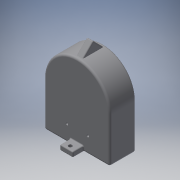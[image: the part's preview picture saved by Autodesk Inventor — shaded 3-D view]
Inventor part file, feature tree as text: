
AUTODESK INVENTOR PART (.ipt)
format: ipt  version: 2018 (Build 220112000, 112)  size: 288,768 bytes
history: native  units: in
note: dims shown in document units (in); Inventor stores cm internally (conversion verified against a paired STEP export)
features: fillet x9, extrude x7, sketch x6, reference x4, plane x1
ambient origin geometry x8: Origin, YZ Plane, XZ Plane, XY Plane, X Axis, Y Axis, Z Axis, Center Point
bodies: Solid1 (feature_tree)
feature tree (27):
  extrude  "Extrusion1"  Depth=1.0in TaperAngle=0.0deg
  extrude  "Extrusion4"  Depth=0.4in TaperAngle=0.0deg
  extrude  "Extrusion5"  Depth=0.1772in
  extrude  "Extrusion6"  Depth=0.25in
  extrude  "Extrusion8"  Depth=0.197in
  plane  "Work Plane1"
  extrude  "Extrusion9"  Depth=0.5in
  extrude  "Extrusion10"  Depth=0.25in
  fillet  "Fillet1"  Radius=0.5in
  fillet  "Fillet2"  Radius=0.197in
  fillet  "Fillet3"  Radius=0.15in
  fillet  "Fillet4"  Radius=0.1378in
  fillet  "Fillet5"  Radius=0.4in
  fillet  "Fillet6"  [1 undecoded]
  fillet  "Fillet7"  Radius=0.1065in
  fillet  "Fillet8"  Radius=0.787in
  fillet  "Fillet9"  Radius=0.394in
  sketch  "Sketch1"  dims[d0=2.5in d1=1.0in d2=0.0in]
  reference  "Reference1"
  sketch  "Sketch2"  dims[d9=0.197in d10=0.4in d11=0.0in]
  reference  "Reference2"
  sketch  "Sketch4"  dims[d12=0.15in d13=0.1772in]
  sketch  "Sketch7"  dims[d14=0.4in d15=0.0in d16=0.25in]
  sketch  "Sketch8"  dims[d17=0.5in d18=0.197in]
  sketch  "Sketch9"  dims[d19=0.4in d20=0.0in d25=0.5in d26=0.25in d27=0.5in d28=0.197in d29=0.15in d30=0.1378in d31=0.4in d32=0.0in d33=-1.25in d34=0.1065in d35=0.787in d36=0.394in d37=0.394in d38=0.25in d39=0.0in d40=0.0787in d41=0.0787in d42=1.0in d43=0.0in d44=0.098in d45=0.0787in d46=0.0787in d47=0.0394in d48=0.0394in d49=0.0394in d50=0.0394in d51=0.0394in d52=0.0394in d53=0.0787in]
  reference  "Reference3"
  reference  "Reference4"
note: 1 required parameter value undecoded (feature->parameter linkage not recoverable at this tier; creation-order binding heuristic only, values carry confidence <= 0.55)
